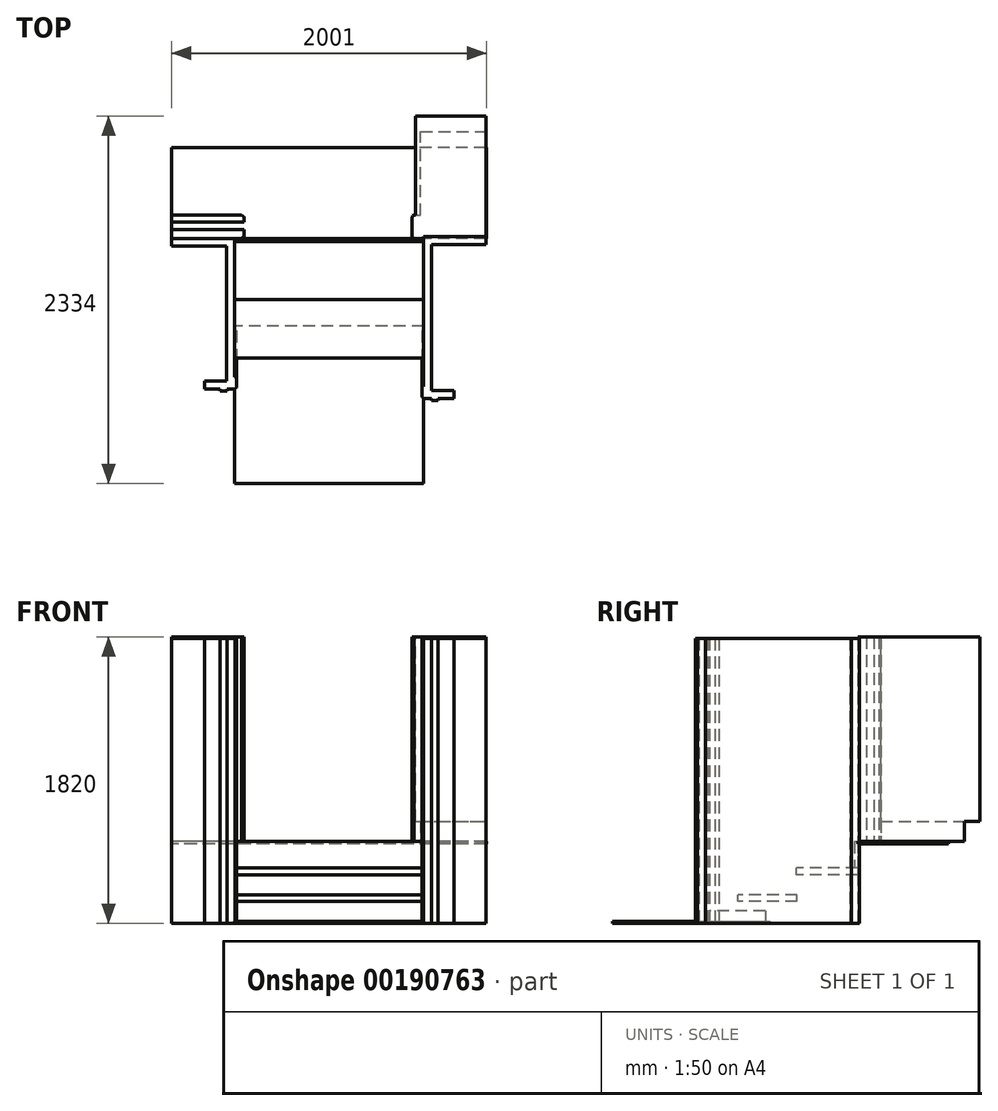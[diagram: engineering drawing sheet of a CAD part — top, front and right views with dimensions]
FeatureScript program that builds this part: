
annotation { "Feature Type Name" : "Feature", "Feature Type Description" : "" }
export const myFeature = defineFeature(function(context is Context, id is Id, definition is map)
    precondition{}
    {
        {
            var Q0;
            Q0=qCreatedBy(makeId("Right.planeOp"),FACE);
            var sketch = newSketch(context, id + "F0", { "sketchPlane" : qUnion([Q0])});
            skLineSegment(sketch, "E0.bottom", {"start": v(0, 0) * mm, "end": v(20, 0) * mm});
            skLineSegment(sketch, "E0.top", {"start": v(0, -168.33) * mm, "end": v(20, -168.33) * mm});
            skLineSegment(sketch, "E0.left", {"start": v(0, 0) * mm, "end": v(0, -168.33) * mm});
            skLineSegment(sketch, "E0.right", {"start": v(20, 0) * mm, "end": v(20, -168.33) * mm});
            skLineSegment(sketch, "E1.bottom", {"start": v(20, -168.33) * mm, "end": v(-276, -168.33) * mm});
            skLineSegment(sketch, "E1.top", {"start": v(20, -211.33) * mm, "end": v(-276, -211.33) * mm});
            skLineSegment(sketch, "E1.left", {"start": v(20, -168.33) * mm, "end": v(20, -211.33) * mm});
            skLineSegment(sketch, "E1.right", {"start": v(-276, -168.33) * mm, "end": v(-276, -211.33) * mm});
            skLineSegment(sketch, "E2.bottom", {"start": v(-272, -211.33) * mm, "end": v(-252, -211.33) * mm});
            skLineSegment(sketch, "E2.top", {"start": v(-272, -379.67) * mm, "end": v(-252, -379.67) * mm});
            skLineSegment(sketch, "E2.left", {"start": v(-272, -211.33) * mm, "end": v(-272, -379.67) * mm});
            skLineSegment(sketch, "E2.right", {"start": v(-252, -211.33) * mm, "end": v(-252, -379.67) * mm});
            skLineSegment(sketch, "E3.bottom", {"start": v(-272, -379.67) * mm, "end": v(-562, -379.67) * mm});
            skLineSegment(sketch, "E3.top", {"start": v(-272, -336.67) * mm, "end": v(-562, -336.67) * mm});
            skLineSegment(sketch, "E3.left", {"start": v(-272, -379.67) * mm, "end": v(-272, -336.67) * mm});
            skLineSegment(sketch, "E3.right", {"start": v(-562, -379.67) * mm, "end": v(-562, -336.67) * mm});
            skLineSegment(sketch, "E4.bottom", {"start": v(-557, -379.67) * mm, "end": v(-537, -379.67) * mm});
            skLineSegment(sketch, "E4.top", {"start": v(-557, -505) * mm, "end": v(-537, -505) * mm});
            skLineSegment(sketch, "E4.left", {"start": v(-557, -379.67) * mm, "end": v(-557, -505) * mm});
            skLineSegment(sketch, "E4.right", {"start": v(-537, -379.67) * mm, "end": v(-537, -505) * mm});
            skLineSegment(sketch, "E5.bottom", {"start": v(20, 0) * mm, "end": v(597, 0) * mm});
            skLineSegment(sketch, "E5.top", {"start": v(20, -15) * mm, "end": v(597, -15) * mm});
            skLineSegment(sketch, "E5.left", {"start": v(20, 0) * mm, "end": v(20, -15) * mm});
            skLineSegment(sketch, "E5.right", {"start": v(597, 0) * mm, "end": v(597, -15) * mm});
            skLineSegment(sketch, "E6.bottom", {"start": v(-537, -505) * mm, "end": v(-1537, -505) * mm});
            skLineSegment(sketch, "E6.top", {"start": v(-537, -520) * mm, "end": v(-1537, -520) * mm});
            skLineSegment(sketch, "E6.left", {"start": v(-537, -505) * mm, "end": v(-537, -520) * mm});
            skLineSegment(sketch, "E6.right", {"start": v(-1537, -505) * mm, "end": v(-1537, -520) * mm});
            skLineSegment(sketch, "E7", {"start": v(134.56, 0) * mm, "end": v(134.56, -168.33) * mm, "construction": true});
            skLineSegment(sketch, "E8", {"start": v(134.56, -168.33) * mm, "end": v(134.56, -336.67) * mm, "construction": true});
            skLineSegment(sketch, "E9", {"start": v(134.56, -336.67) * mm, "end": v(134.56, -505) * mm, "construction": true});
            skPoint(sketch, "E9.endSnap0", {"position": v(-547, -505) * mm});
            skLineSegment(sketch, "E10", {"start": v(20, -168.33) * mm, "end": v(172.47, -168.33) * mm, "construction": true});
            skLineSegment(sketch, "E11", {"start": v(-272, -336.67) * mm, "end": v(193.86, -336.67) * mm, "construction": true});
            skLineSegment(sketch, "E12", {"start": v(-537, -505) * mm, "end": v(230.7, -505) * mm, "construction": true});
            skSolve(sketch);
        }
        {
            var Q0;
            Q0=makeQuery(id+"F0.imprint","IMPRINT",FACE,{"disambiguationData":[TD([[makeQuery(id+"F0.imprint","IMPRINT",EDGE,{"derivedFrom":sQuery(id+"F0.wireOp",EDGE,"E6.top")}),-1.0]])]});
            extrude(context, id + "F1", {"entities" : qUnion([Q0]), "endBound" : BoundingType.SYMMETRIC, "depth" : 1200 * mm});
        }
        {
            var Q0;
            Q0=makeQuery(id+"F0.imprint","IMPRINT",FACE,{"disambiguationData":[TD([[makeQuery(id+"F0.imprint","IMPRINT",EDGE,{"derivedFrom":sQuery(id+"F0.wireOp",EDGE,"E5.bottom")}),-1.0]])]});
            extrude(context, id + "F2", {"entities" : qUnion([Q0]), "endBound" : BoundingType.SYMMETRIC, "depth" : 2000 * mm});
        }
        {
            var Q0;
            Q0=makeQuery(id+"F2.opExtrude","SWEPT_FACE",FACE,{"disambiguationData":[OSD([sQuery(id+"F0.wireOp",EDGE,"E5.bottom")])]});
            var sketch = newSketch(context, id + "F3", { "sketchPlane" : qUnion([Q0])});
            skLineSegment(sketch, "E13.bottom", {"start": v(600, 20) * mm, "end": v(540, 20) * mm});
            skLineSegment(sketch, "E13.top", {"start": v(600, 31) * mm, "end": v(530, 31) * mm});
            skLineSegment(sketch, "E13.left", {"start": v(600, 20) * mm, "end": v(600, 31) * mm});
            skLineSegment(sketch, "E13.right", {"start": v(530, 28) * mm, "end": v(530, 31) * mm});
            skLineSegment(sketch, "E14", {"start": v(540, 20) * mm, "end": v(530, 28) * mm});
            skLineSegment(sketch, "E15", {"start": v(530, 31) * mm, "end": v(525, 31) * mm});
            skLineSegment(sketch, "E16", {"start": v(525, 31) * mm, "end": v(525, 156) * mm});
            skLineSegment(sketch, "E17", {"start": v(525, 156) * mm, "end": v(530, 156) * mm});
            skLineSegment(sketch, "E18", {"start": v(530, 156) * mm, "end": v(530, 164) * mm});
            skLineSegment(sketch, "E19", {"start": v(530, 164) * mm, "end": v(540, 167) * mm});
            skLineSegment(sketch, "E20", {"start": v(540, 167) * mm, "end": v(580, 167) * mm});
            skLineSegment(sketch, "E21", {"start": v(580, 167) * mm, "end": v(580, 697) * mm});
            skLineSegment(sketch, "E22", {"start": v(580, 697) * mm, "end": v(995, 697) * mm});
            skLineSegment(sketch, "E23", {"start": v(995, 697) * mm, "end": v(995, 31) * mm});
            skLineSegment(sketch, "E24", {"start": v(995, 31) * mm, "end": v(600, 31) * mm});
            skLineSegment(sketch, "E25", {"start": v(-600, 20) * mm, "end": v(-556, 20) * mm});
            skLineSegment(sketch, "E26", {"start": v(-556, 20) * mm, "end": v(-546, 28) * mm});
            skLineSegment(sketch, "E27", {"start": v(-546, 28) * mm, "end": v(-546, 31) * mm});
            skLineSegment(sketch, "E28", {"start": v(-546, 31) * mm, "end": v(-541, 31) * mm});
            skLineSegment(sketch, "E29", {"start": v(-541, 31) * mm, "end": v(-541, 76) * mm});
            skLineSegment(sketch, "E30", {"start": v(-541, 76) * mm, "end": v(-1001, 76) * mm});
            skLineSegment(sketch, "E31", {"start": v(-1001, 76) * mm, "end": v(-1001, 20) * mm});
            skLineSegment(sketch, "E32", {"start": v(-541, 76) * mm, "end": v(-541, 124) * mm, "construction": true});
            skLineSegment(sketch, "E33", {"start": v(-1001, 20) * mm, "end": v(-556, 20) * mm});
            skPoint(sketch, "E34.endSnap0", {"position": v(-541, 100) * mm});
            skLineSegment(sketch, "E35.MirrorCS", {"start": v(-546, 157) * mm, "end": v(-541, 157) * mm});
            skLineSegment(sketch, "E36.MirrorCS", {"start": v(-556, 168) * mm, "end": v(-546, 160) * mm});
            skLineSegment(sketch, "E37.MirrorCS", {"start": v(-546, 160) * mm, "end": v(-546, 157) * mm});
            skLineSegment(sketch, "E38.MirrorCS", {"start": v(-600, 168) * mm, "end": v(-556, 168) * mm});
            skLineSegment(sketch, "E39.MirrorCS", {"start": v(-541, 124) * mm, "end": v(-1001, 124) * mm});
            skLineSegment(sketch, "E40.MirrorCS", {"start": v(-1001, 168) * mm, "end": v(-556, 168) * mm});
            skLineSegment(sketch, "E41.MirrorCS", {"start": v(-1001, 124) * mm, "end": v(-1001, 168) * mm});
            skLineSegment(sketch, "E42.MirrorCS", {"start": v(-541, 157) * mm, "end": v(-541, 124) * mm});
            skLineSegment(sketch, "E43", {"start": v(-556, 20) * mm, "end": v(-556, 168) * mm, "construction": true});
            skLineSegment(sketch, "E44", {"start": v(-546, 31) * mm, "end": v(-546, 157) * mm, "construction": true});
            skLineSegment(sketch, "E45", {"start": v(-1001, 76) * mm, "end": v(-1001, 124) * mm, "construction": true});
            skLineSegment(sketch, "E46", {"start": v(580, 167) * mm, "end": v(995, 167) * mm});
            skSolve(sketch);
        }
        {
            var Q0;
            {var subQ0=sQuery(id+"F3.wireOp",EDGE,"E26");Q0=makeQuery(id+"F3.imprint","IMPRINT",FACE,{"disambiguationData":[TD([[makeQuery(id+"F3.imprint","IMPRINT",EDGE,{"derivedFrom":subQ0}),1.0]])]});}
            var Q1;
            Q1=makeQuery(id+"F3.imprint","IMPRINT",FACE,{"disambiguationData":[TD([[makeQuery(id+"F3.imprint","IMPRINT",EDGE,{"derivedFrom":sQuery(id+"F3.wireOp",EDGE,"E35.MirrorCS")}),-1.0]])]});
            var Q2;
            Q2=makeQuery(id+"F3.imprint","IMPRINT",FACE,{"disambiguationData":[TD([[makeQuery(id+"F3.imprint","IMPRINT",EDGE,{"derivedFrom":sQuery(id+"F3.wireOp",EDGE,"E13.top")}),-1.0]])]});
            var Q3;
            {var subQ0=sQuery(id+"F3.wireOp",EDGE,"E46");Q3=makeQuery(id+"F3.imprint","IMPRINT",FACE,{"disambiguationData":[TD([[makeQuery(id+"F3.imprint","IMPRINT",EDGE,{"derivedFrom":subQ0}),1.0]])]});}
            var Q4;
            {var subQ0=sQuery(id+"F3.wireOp",EDGE,"E22");Q4=makeQuery(id+"F3.imprint","IMPRINT",FACE,{"disambiguationData":[TD([[makeQuery(id+"F3.imprint","IMPRINT",EDGE,{"derivedFrom":subQ0}),-1.0]])]});}
            var Q5;
            Q5=makeQuery(id+"F3.imprint","IMPRINT",FACE,{"disambiguationData":[TD([[makeQuery(id+"F3.imprint","IMPRINT",EDGE,{"derivedFrom":sQuery(id+"F3.wireOp",EDGE,"E13.bottom")}),-1.0]])]});
            extrude(context, id + "F4", {"entities" : qUnion([Q0, Q1, Q2, Q3, Q4, Q5]), "depth" : 1300 * mm});
        }
        {
            var Q0;
            Q0=makeQuery(id+"F4.opExtrude","CAP_FACE",FACE,{"disambiguationData":[OSD([sQuery(id+"F3.wireOp",EDGE,"E13.top"),sQuery(id+"F3.wireOp",EDGE,"E15"),sQuery(id+"F3.wireOp",EDGE,"E16"),sQuery(id+"F3.wireOp",EDGE,"E17"),sQuery(id+"F3.wireOp",EDGE,"E18"),sQuery(id+"F3.wireOp",EDGE,"E19"),sQuery(id+"F3.wireOp",EDGE,"E20"),sQuery(id+"F3.wireOp",EDGE,"E21"),sQuery(id+"F3.wireOp",EDGE,"E22"),sQuery(id+"F3.wireOp",EDGE,"E23"),sQuery(id+"F3.wireOp",EDGE,"E24")])],"isStart":false});
            var sketch = newSketch(context, id + "F5", { "sketchPlane" : qUnion([Q0])});
            skLineSegment(sketch, "E47", {"start": v(550, 167) * mm, "end": v(550, 797) * mm});
            skLineSegment(sketch, "E48", {"start": v(550, 797) * mm, "end": v(995, 797) * mm});
            skLineSegment(sketch, "E49", {"start": v(995, 797) * mm, "end": v(995, 164) * mm});
            skLineSegment(sketch, "E50", {"start": v(995, 164) * mm, "end": v(550, 167) * mm});
            skSolve(sketch);
        }
        {
            var Q0;
            {var subQ4=sQuery(id+"F5.wireOp",EDGE,"E47");Q0=makeQuery(id+"F5.imprint","IMPRINT",FACE,{"disambiguationData":[TD([[makeQuery(id+"F5.imprint","IMPRINT",EDGE,{"derivedFrom":subQ4}),-1.0]])]});}
            extrude(context, id + "F6", {"entities" : qUnion([Q0]), "operationType" : NewBodyOperationType.ADD, "oppositeDirection" : true, "depth" : 1170 * mm});
        }
        {
            var Q0;
            Q0=makeQuery(id+"F1.opExtrude","SWEPT_FACE",FACE,{"disambiguationData":[OSD([sQuery(id+"F0.wireOp",EDGE,"E6.top")])]});
            cPlane(context, id + "F7", {"entities" : qUnion([Q0]), "cplaneType" : CPlaneType.OFFSET, "offset" : 0 * mm, "width" : 150 * mm, "height" : 150 * mm});
        }
        {
            var Q0;
            Q0=qCreatedBy(id+"F7.planeOp",FACE);
            var sketch = newSketch(context, id + "F8", { "sketchPlane" : qUnion([Q0])});
            skLineSegment(sketch, "E51.0", {"start": v(995, -31) * mm, "end": v(600, -31) * mm});
            skLineSegment(sketch, "E52", {"start": v(600, -31) * mm, "end": v(600, 922) * mm});
            skLineSegment(sketch, "E53", {"start": v(600, 922) * mm, "end": v(589, 922) * mm});
            skLineSegment(sketch, "E54", {"start": v(589, 922) * mm, "end": v(589, 987) * mm});
            skLineSegment(sketch, "E55", {"start": v(589, 987) * mm, "end": v(599, 994) * mm});
            skLineSegment(sketch, "E56", {"start": v(599, 994) * mm, "end": v(599, 997) * mm});
            skLineSegment(sketch, "E57", {"start": v(599, 997) * mm, "end": v(649, 997) * mm});
            skLineSegment(sketch, "E58", {"start": v(649, 997) * mm, "end": v(649, 1010) * mm});
            skLineSegment(sketch, "E59", {"start": v(649, 1010) * mm, "end": v(692, 1010) * mm});
            skLineSegment(sketch, "E60", {"start": v(692, 1010) * mm, "end": v(692, 997) * mm});
            skLineSegment(sketch, "E61", {"start": v(692, 997) * mm, "end": v(792, 997) * mm});
            skLineSegment(sketch, "E62", {"start": v(792, 997) * mm, "end": v(792, 947) * mm});
            skLineSegment(sketch, "E63", {"start": v(792, 947) * mm, "end": v(650, 947) * mm});
            skLineSegment(sketch, "E64", {"start": v(650, 947) * mm, "end": v(650, 19) * mm});
            skLineSegment(sketch, "E65", {"start": v(650, 19) * mm, "end": v(995, 19) * mm});
            skLineSegment(sketch, "E66", {"start": v(995, 19) * mm, "end": v(995, -31) * mm});
            skPoint(sketch, "E67.0", {"position": v(600, 567) * mm});
            skLineSegment(sketch, "E68", {"start": v(600, 567) * mm, "end": v(589, 567) * mm});
            skLineSegment(sketch, "E69", {"start": v(589, 567) * mm, "end": v(589, 922) * mm});
            skPoint(sketch, "E70.0", {"position": v(-1001, -20) * mm});
            skPoint(sketch, "E71.0", {"position": v(-600, -20) * mm});
            skLineSegment(sketch, "E72", {"start": v(-1001, -20) * mm, "end": v(-600, -20) * mm});
            skLineSegment(sketch, "E73", {"start": v(-600, 862) * mm, "end": v(-589, 862) * mm});
            skLineSegment(sketch, "E74", {"start": v(-589, 862) * mm, "end": v(-589, 927) * mm});
            skLineSegment(sketch, "E75", {"start": v(-589, 927) * mm, "end": v(-599, 934) * mm});
            skLineSegment(sketch, "E76", {"start": v(-599, 934) * mm, "end": v(-599, 937) * mm});
            skLineSegment(sketch, "E77", {"start": v(-599, 937) * mm, "end": v(-649, 937) * mm});
            skLineSegment(sketch, "E78", {"start": v(-649, 937) * mm, "end": v(-649, 950) * mm});
            skLineSegment(sketch, "E79", {"start": v(-649, 950) * mm, "end": v(-692, 950) * mm});
            skLineSegment(sketch, "E80", {"start": v(-692, 950) * mm, "end": v(-692, 937) * mm});
            skLineSegment(sketch, "E81", {"start": v(-692, 937) * mm, "end": v(-792, 937) * mm});
            skLineSegment(sketch, "E82", {"start": v(-792, 937) * mm, "end": v(-792, 887) * mm});
            skLineSegment(sketch, "E83", {"start": v(-792, 887) * mm, "end": v(-650, 887) * mm});
            skLineSegment(sketch, "E84", {"start": v(-650, 887) * mm, "end": v(-650, 30) * mm});
            skLineSegment(sketch, "E85", {"start": v(-650, 30) * mm, "end": v(-1001, 30) * mm});
            skLineSegment(sketch, "E86", {"start": v(-1001, 30) * mm, "end": v(-1001, -20) * mm});
            skPoint(sketch, "E87.0", {"position": v(-600, 567) * mm});
            skLineSegment(sketch, "E88", {"start": v(-600, 567) * mm, "end": v(-589, 567) * mm});
            skLineSegment(sketch, "E89", {"start": v(-589, 567) * mm, "end": v(-589, 862) * mm});
            skLineSegment(sketch, "E90", {"start": v(-600, -20) * mm, "end": v(-600, 862) * mm});
            skSolve(sketch);
        }
        {
            var Q0;
            {var subQ1=sQuery(id+"F8.wireOp",EDGE,"E51.0");Q0=makeQuery(id+"F8.imprint","IMPRINT",FACE,{"disambiguationData":[TD([[makeQuery(id+"F8.imprint","IMPRINT",EDGE,{"derivedFrom":subQ1}),-1.0]])]});}
            var Q1;
            {var subQ0=sQuery(id+"F8.wireOp",EDGE,"E72");Q1=makeQuery(id+"F8.imprint","IMPRINT",FACE,{"disambiguationData":[TD([[makeQuery(id+"F8.imprint","IMPRINT",EDGE,{"derivedFrom":subQ0}),1.0]])]});}
            extrude(context, id + "F9", {"entities" : qUnion([Q0, Q1]), "oppositeDirection" : true, "depth" : 1810 * mm});
        }
        {
            var Q0;
            {var subQ0=sQuery(id+"F8.wireOp",EDGE,"E53");Q0=makeQuery(id+"F8.imprint","IMPRINT",FACE,{"disambiguationData":[TD([[makeQuery(id+"F8.imprint","IMPRINT",EDGE,{"derivedFrom":subQ0}),1.0]])]});}
            var Q1;
            {var subQ0=sQuery(id+"F8.wireOp",EDGE,"E73");Q1=makeQuery(id+"F8.imprint","IMPRINT",FACE,{"disambiguationData":[TD([[makeQuery(id+"F8.imprint","IMPRINT",EDGE,{"derivedFrom":subQ0}),-1.0]])]});}
            extrude(context, id + "F10", {"entities" : qUnion([Q0, Q1]), "oppositeDirection" : true, "depth" : 80 * mm});
        }
        {
            var Q0;
            Q0=makeQuery(id+"F9.opExtrude","SWEPT_FACE",FACE,{"disambiguationData":[OSD([sQuery(id+"F8.wireOp",EDGE,"E90")])]});
            var sketch = newSketch(context, id + "F11", { "sketchPlane" : qUnion([Q0])});
            skLineSegment(sketch, "E91", {"start": v(-1110.69, -505) * mm, "end": v(-1110.69, 0) * mm, "construction": true});
            skLineSegment(sketch, "E92.0", {"start": v(-537, -505) * mm, "end": v(-1537, -505) * mm});
            skPoint(sketch, "E93.orphan", {"position": v(-365.23, -379.67) * mm});
            skLineSegment(sketch, "E94", {"start": v(-562, -505) * mm, "end": v(-1110.69, -505) * mm, "construction": true});
            skLineSegment(sketch, "E95.bottom", {"start": v(20, -211.33) * mm, "end": v(-370.23, -211.33) * mm});
            skLineSegment(sketch, "E95.top", {"start": v(20, -168.33) * mm, "end": v(-370.23, -168.33) * mm});
            skLineSegment(sketch, "E95.left", {"start": v(20, -211.33) * mm, "end": v(20, -168.33) * mm});
            skLineSegment(sketch, "E95.right", {"start": v(-370.23, -211.33) * mm, "end": v(-370.23, -168.33) * mm});
            skLineSegment(sketch, "E96.bottom", {"start": v(-365.23, -379.67) * mm, "end": v(-740.46, -379.67) * mm});
            skLineSegment(sketch, "E96.top", {"start": v(-365.23, -336.67) * mm, "end": v(-740.46, -336.67) * mm});
            skLineSegment(sketch, "E96.left", {"start": v(-365.23, -379.67) * mm, "end": v(-365.23, -336.67) * mm});
            skLineSegment(sketch, "E96.right", {"start": v(-740.46, -379.67) * mm, "end": v(-740.46, -336.67) * mm});
            skLineSegment(sketch, "E97.bottom", {"start": v(-365.23, -211.33) * mm, "end": v(-346.23, -211.33) * mm});
            skLineSegment(sketch, "E97.top", {"start": v(-365.23, -379.67) * mm, "end": v(-346.23, -379.67) * mm});
            skLineSegment(sketch, "E97.left", {"start": v(-365.23, -211.33) * mm, "end": v(-365.23, -379.67) * mm});
            skLineSegment(sketch, "E97.right", {"start": v(-346.23, -211.33) * mm, "end": v(-346.23, -379.67) * mm});
            skLineSegment(sketch, "E98.bottom", {"start": v(-735.46, -379.67) * mm, "end": v(-716.46, -379.67) * mm});
            skLineSegment(sketch, "E98.top", {"start": v(-735.46, -505) * mm, "end": v(-716.46, -505) * mm});
            skLineSegment(sketch, "E98.left", {"start": v(-735.46, -379.67) * mm, "end": v(-735.46, -505) * mm});
            skLineSegment(sketch, "E98.right", {"start": v(-716.46, -379.67) * mm, "end": v(-716.46, -505) * mm});
            skLineSegment(sketch, "E99", {"start": v(142.5, 0) * mm, "end": v(142.5, -168.33) * mm, "construction": true});
            skLineSegment(sketch, "E100", {"start": v(142.5, -168.33) * mm, "end": v(142.5, -336.67) * mm, "construction": true});
            skLineSegment(sketch, "E101", {"start": v(142.5, -336.67) * mm, "end": v(142.5, -505) * mm, "construction": true});
            skLineSegment(sketch, "E102", {"start": v(0, 0) * mm, "end": v(-1110.69, 0) * mm, "construction": true});
            skLineSegment(sketch, "E103", {"start": v(0, 0) * mm, "end": v(-1110.69, -505) * mm, "construction": true});
            skLineSegment(sketch, "E104.0.0", {"start": v(-947, -520) * mm, "end": v(-19, -520) * mm});
            skLineSegment(sketch, "E104.0.1", {"start": v(-19, -520) * mm, "end": v(-19, 1290) * mm});
            skLineSegment(sketch, "E104.0.2", {"start": v(-19, 1290) * mm, "end": v(-947, 1290) * mm});
            skLineSegment(sketch, "E104.0.3", {"start": v(-947, 1290) * mm, "end": v(-947, -520) * mm});
            skLineSegment(sketch, "E105.0", {"start": v(20, 0) * mm, "end": v(20, -168.33) * mm});
            skLineSegment(sketch, "E105.1", {"start": v(0, 0) * mm, "end": v(0, -168.33) * mm});
            skLineSegment(sketch, "E105.2", {"start": v(0, 0) * mm, "end": v(20, 0) * mm});
            skLineSegment(sketch, "E106", {"start": v(0, -168.33) * mm, "end": v(20, -168.33) * mm});
            skSolve(sketch);
        }
        {
            var Q0;
            {var subQ0=sQuery(id+"F11.wireOp",EDGE,"E95.right");Q0=makeQuery(id+"F11.imprint","IMPRINT",FACE,{"disambiguationData":[TD([[makeQuery(id+"F11.imprint","IMPRINT",EDGE,{"derivedFrom":subQ0}),-1.0]])]});}
            var Q1;
            {var subQ1=sQuery(id+"F11.wireOp",EDGE,"E96.top");Q1=makeQuery(id+"F11.imprint","IMPRINT",FACE,{"disambiguationData":[TD([[makeQuery(id+"F11.imprint","IMPRINT",EDGE,{"derivedFrom":subQ1}),1.0]])]});}
            var Q2;
            {var subQ6=sQuery(id+"F11.wireOp",EDGE,"E95.left");Q2=makeQuery(id+"F11.imprint","IMPRINT",FACE,{"disambiguationData":[TD([[makeQuery(id+"F11.imprint","IMPRINT",EDGE,{"derivedFrom":subQ6}),-1.0]])]});}
            extrude(context, id + "F12", {"entities" : qUnion([Q0, Q1, Q2]), "depth" : 1200 * mm});
        }
        {
            var Q0;
            Q0=makeQuery(id+"F10.opExtrude","SWEPT_BODY",BODY,{"disambiguationData":[OSD([sQuery(id+"F8.wireOp",EDGE,"E73"),sQuery(id+"F8.wireOp",EDGE,"E88"),sQuery(id+"F8.wireOp",EDGE,"E89"),sQuery(id+"F8.wireOp",EDGE,"E90")])]});
            var Q1;
            Q1=makeQuery(id+"F10.opExtrude","SWEPT_BODY",BODY,{"disambiguationData":[OSD([sQuery(id+"F8.wireOp",EDGE,"E52"),sQuery(id+"F8.wireOp",EDGE,"E53"),sQuery(id+"F8.wireOp",EDGE,"E68"),sQuery(id+"F8.wireOp",EDGE,"E69")])]});
            var Q2;
            Q2=makeQuery(id+"F12.opExtrude","SWEPT_BODY",BODY,{"disambiguationData":[OSD([sQuery(id+"F11.wireOp",EDGE,"E96.bottom"),sQuery(id+"F11.wireOp",EDGE,"E96.top"),sQuery(id+"F11.wireOp",EDGE,"E96.left"),sQuery(id+"F11.wireOp",EDGE,"E96.right"),sQuery(id+"F11.wireOp",EDGE,"E98.top"),sQuery(id+"F11.wireOp",EDGE,"E98.left"),sQuery(id+"F11.wireOp",EDGE,"E98.right")])]});
            booleanBodies(context, id + "F13", {"operationType" : BooleanOperationType.SUBTRACTION, "tools" : qUnion([Q0, Q1]), "targets" : qUnion([Q2]), "keepTools" : true});
        }
        {
            var Q0;
            Q0=makeQuery(id+"F11.imprint","IMPRINT",FACE,{"disambiguationData":[TD([[makeQuery(id+"F11.imprint","IMPRINT",EDGE,{"derivedFrom":sQuery(id+"F11.wireOp",EDGE,"E105.0")}),-1.0]])]});
            var Q1;
            {var subQ2=sQuery(id+"F11.wireOp",EDGE,"E97.bottom");Q1=makeQuery(id+"F11.imprint","IMPRINT",FACE,{"disambiguationData":[TD([[makeQuery(id+"F11.imprint","IMPRINT",EDGE,{"derivedFrom":subQ2}),-1.0]])]});}
            var Q2;
            Q2=makeQuery(id+"F11.imprint","IMPRINT",FACE,{"disambiguationData":[TD([[makeQuery(id+"F11.imprint","IMPRINT",EDGE,{"derivedFrom":sQuery(id+"F11.wireOp",EDGE,"E98.bottom")}),-1.0]])]});
            extrude(context, id + "F14", {"entities" : qUnion([Q0, Q1, Q2]), "depth" : 1199 * mm});
        }
    });
